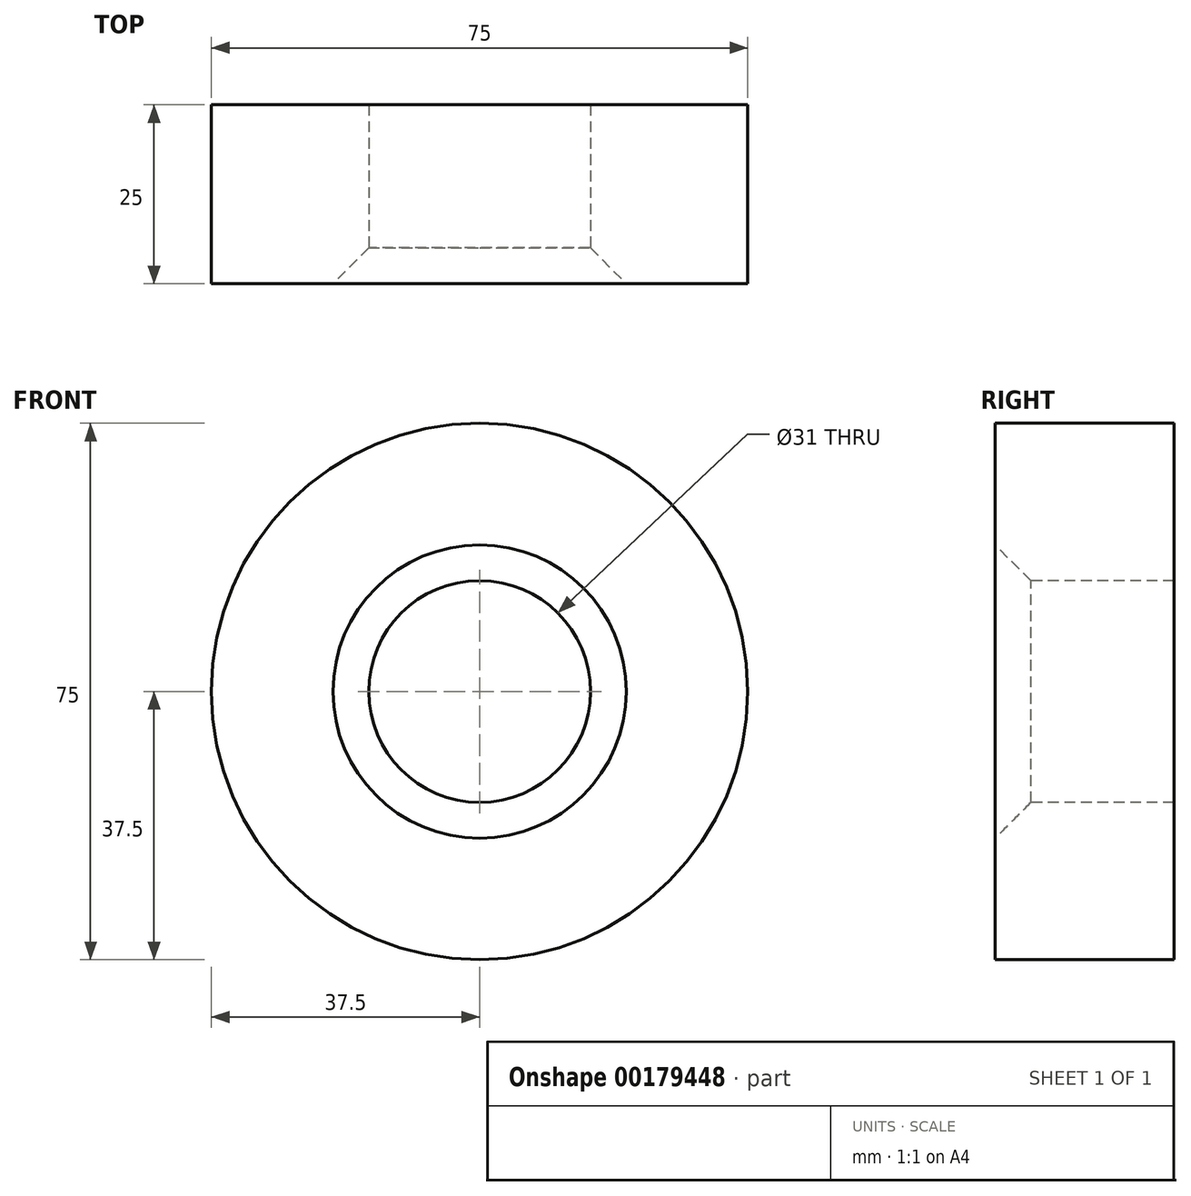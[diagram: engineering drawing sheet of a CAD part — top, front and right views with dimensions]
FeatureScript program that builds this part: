
annotation { "Feature Type Name" : "Feature", "Feature Type Description" : "" }
export const myFeature = defineFeature(function(context is Context, id is Id, definition is map)
    precondition{}
    {
        {
            var Q0;
            Q0=qCreatedBy(makeId("Front.planeOp"),FACE);
            var sketch = newSketch(context, id + "F0", { "sketchPlane" : qUnion([Q0])});
            skCircle(sketch, "E0", {"center": v(0, 0) * mm, "radius": 37.5 * mm});
            skCircle(sketch, "E1", {"center": v(0, 0) * mm, "radius": 15.5 * mm});
            skSolve(sketch);
        }
        {
            var Q0;
            Q0 = qSketchRegion(id + "F0", true);
            extrude(context, id + "F1", {"entities" : qUnion([Q0]), "oppositeDirection" : true, "depth" : 25 * mm});
        }
        {
            var Q0;
            Q0=makeQuery(id+"F1.opExtrude","CAP_EDGE",EDGE,{"disambiguationData":[OSD([sQuery(id+"F0.wireOp",EDGE,"E1")])],"isStart":true});
            chamfer(context, id + "F2", {"entities" : qUnion([Q0]), "width" : 5 * mm, "tangentPropagation" : true});
        }
    });
